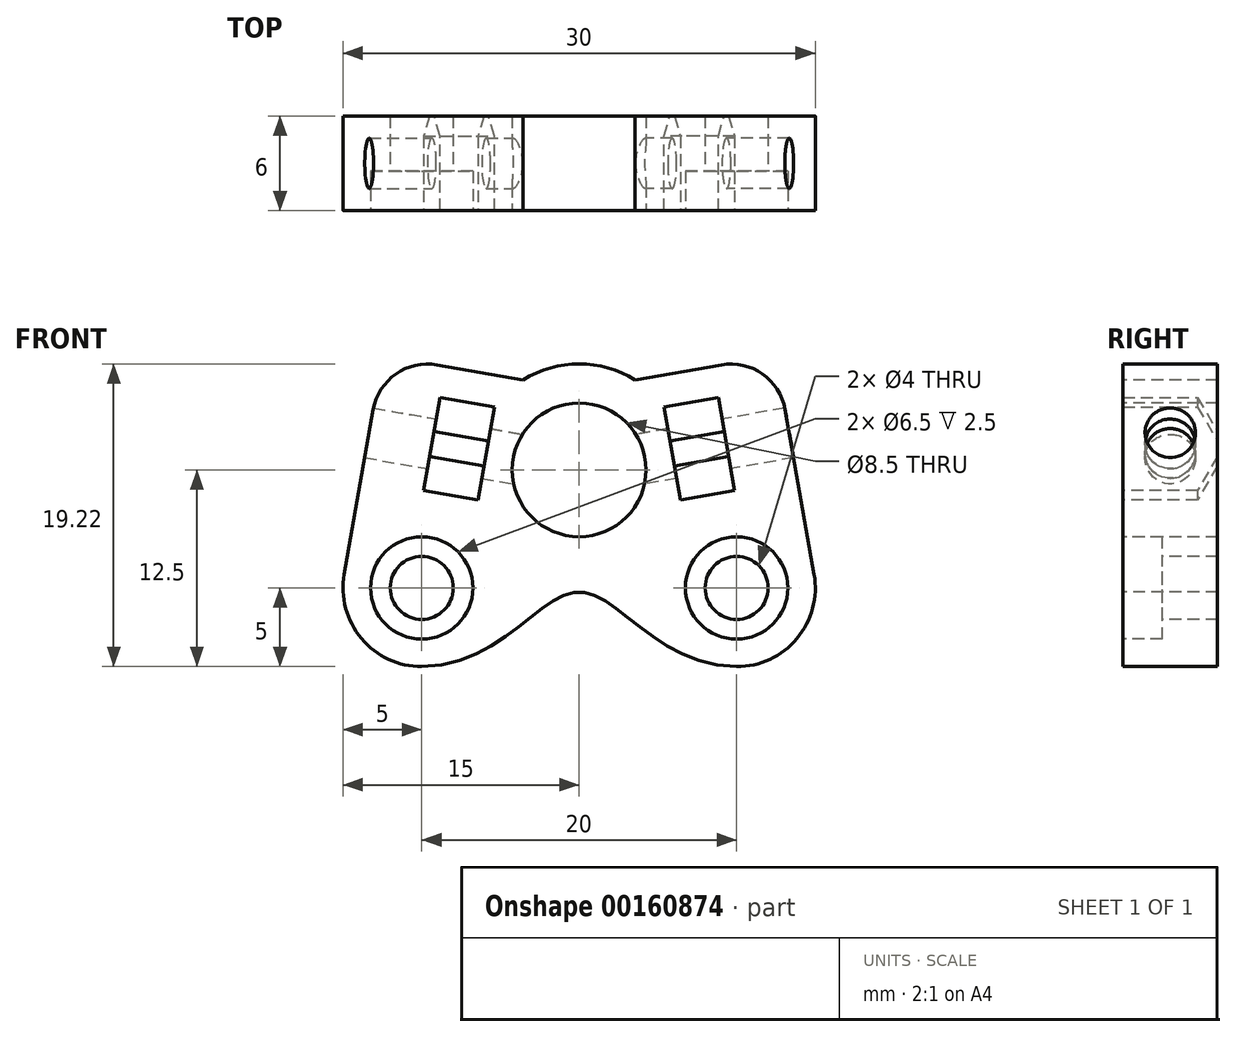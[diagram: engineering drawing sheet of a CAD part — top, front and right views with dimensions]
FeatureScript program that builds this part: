
annotation { "Feature Type Name" : "Feature", "Feature Type Description" : "" }
export const myFeature = defineFeature(function(context is Context, id is Id, definition is map)
    precondition{}
    {
        {
            var Q0;
            Q0=qCreatedBy(makeId("Front.planeOp"),FACE);
            var sketch = newSketch(context, id + "F0", { "sketchPlane" : qUnion([Q0])});
            skCircle(sketch, "E0", {"center": v(0, 0) * mm, "radius": 4.25 * mm});
            skCircle(sketch, "E1", {"center": v(-10, -7.5) * mm, "radius": 2 * mm});
            skCircle(sketch, "E2.MirrorC", {"center": v(10, -7.5) * mm, "radius": 2 * mm});
            skFitSpline(sketch, "E3", {"points": [v(10, -12.5) * mm, v(0, -7.75) * mm, v(-10, -12.5) * mm], "startDerivative": vector(-30, 0) * mm, "endDerivative": vector(-30, 0) * mm});
            skArc(sketch, "E4", {"start": v(10, -12.5) * mm, "mid": v(13.83, -10.71) * mm, "end": v(14.92, -6.63) * mm});
            skLineSegment(sketch, "E5", {"start": v(13.08, 3.83) * mm, "end": v(13.34, 2.35) * mm});
            skLineSegment(sketch, "E6", {"start": v(13.34, 2.35) * mm, "end": v(14.92, -6.63) * mm});
            skLineSegment(sketch, "E7", {"start": v(0, 0) * mm, "end": v(13.34, 2.35) * mm, "construction": true});
            skLineSegment(sketch, "E8.MirrorCS", {"start": v(-13.34, 2.35) * mm, "end": v(-14.92, -6.63) * mm});
            skLineSegment(sketch, "E9", {"start": v(9.02, 6.67) * mm, "end": v(3.56, 5.7) * mm});
            skArc(sketch, "E10", {"start": v(3.56, 5.7) * mm, "mid": v(1.85, 6.46) * mm, "end": v(0, 6.72) * mm});
            skArc(sketch, "E11.MirrorCS", {"start": v(-3.56, 5.7) * mm, "mid": v(-1.85, 6.46) * mm, "end": v(0, 6.72) * mm});
            skPoint(sketch, "E12.visualSharp", {"position": v(12.47, 7.28) * mm});
            skArc(sketch, "E12.filletArc", {"start": v(13.08, 3.83) * mm, "mid": v(11.64, 6.09) * mm, "end": v(9.02, 6.67) * mm});
            skArc(sketch, "E13.MirrorCS", {"start": v(-13.08, 3.83) * mm, "mid": v(-11.64, 6.09) * mm, "end": v(-9.02, 6.67) * mm});
            skLineSegment(sketch, "E14.MirrorCS", {"start": v(-9.02, 6.67) * mm, "end": v(-3.56, 5.7) * mm});
            skLineSegment(sketch, "E15.MirrorCS", {"start": v(-13.08, 3.83) * mm, "end": v(-13.34, 2.35) * mm});
            skLineSegment(sketch, "E16", {"start": v(10, -7.5) * mm, "end": v(14.92, -6.63) * mm, "construction": true});
            skArc(sketch, "E17.MirrorCS", {"start": v(-10, -12.5) * mm, "mid": v(-13.83, -10.71) * mm, "end": v(-14.92, -6.63) * mm});
            skLineSegment(sketch, "E18", {"start": v(0, 6.72) * mm, "end": v(13.48, 6.72) * mm, "construction": true});
            skSolve(sketch);
        }
        {
            var Q0;
            Q0 = qSketchRegion(id + "F0", true);
            extrude(context, id + "F1", {"entities" : qUnion([Q0]), "oppositeDirection" : true, "depth" : 6 * mm});
        }
        {
            var Q0;
            Q0=qCreatedBy(makeId("Right.planeOp"),FACE);
            var sketch = newSketch(context, id + "F2", { "sketchPlane" : qUnion([Q0])});
            skLineSegment(sketch, "E19", {"start": v(-49.69, 0) * mm, "end": v(53.27, 0) * mm, "construction": true});
            skSolve(sketch);
        }
        {
            var Q0;
            Q0=sQuery(id+"F2.wireOp",EDGE,"E19");
            cPlane(context, id + "F3", {"entities" : qUnion([Q0]), "cplaneType" : CPlaneType.LINE_ANGLE, "offset" : 25 * mm, "angle" : 80 * degree, "width" : 150 * mm, "height" : 150 * mm});
        }
        {
            var Q0;
            Q0=qCreatedBy(id+"F3.planeOp",FACE);
            var sketch = newSketch(context, id + "F4", { "sketchPlane" : qUnion([Q0])});
            skCircle(sketch, "E20", {"center": v(3, 0) * mm, "radius": 1.6 * mm});
            skLineSegment(sketch, "E21", {"start": v(0, 0) * mm, "end": v(6, 0) * mm, "construction": true});
            skSolve(sketch);
        }
        {
            var Q0;
            Q0 = qSketchRegion(id + "F4", true);
            extrude(context, id + "F5", {"entities" : qUnion([Q0]), "depth" : 15 * mm});
        }
        {
            var Q0;
            Q0=qCreatedBy(id+"F3.planeOp",FACE);
            cPlane(context, id + "F6", {"entities" : qUnion([Q0]), "cplaneType" : CPlaneType.OFFSET, "offset" : 6 * mm, "width" : 150 * mm, "height" : 150 * mm});
        }
        {
            var Q0;
            Q0=qCreatedBy(id+"F6.planeOp",FACE);
            var sketch = newSketch(context, id + "F7", { "sketchPlane" : qUnion([Q0])});
            skPoint(sketch, "E22", {"position": v(3, 0) * mm});
            skCircle(sketch, "E23.cCircle", {"center": v(3, 0) * mm, "radius": 3 * mm, "construction": true});
            skLineSegment(sketch, "E23.0", {"start": v(4.73, -3) * mm, "end": v(1.27, -3) * mm});
            skLineSegment(sketch, "E23.3", {"start": v(1.27, 3) * mm, "end": v(4.73, 3) * mm});
            skLineSegment(sketch, "E23.4", {"start": v(4.73, 3) * mm, "end": v(6.46, 0) * mm});
            skLineSegment(sketch, "E23.5", {"start": v(6.46, 0) * mm, "end": v(4.73, -3) * mm});
            skPoint(sketch, "E23.0.midPoint", {"position": v(3, -3) * mm});
            skLineSegment(sketch, "E24", {"start": v(1.27, -3) * mm, "end": v(-12.08, -3) * mm});
            skLineSegment(sketch, "E25", {"start": v(-12.08, -3) * mm, "end": v(-12.08, 3) * mm});
            skLineSegment(sketch, "E26", {"start": v(-12.08, 3) * mm, "end": v(1.27, 3) * mm});
            skLineSegment(sketch, "E27", {"start": v(0, 0) * mm, "end": v(6, 0) * mm, "construction": true});
            skSolve(sketch);
        }
        {
            var Q0;
            Q0 = qSketchRegion(id + "F7", true);
            extrude(context, id + "F8", {"entities" : qUnion([Q0]), "depth" : 3.5 * mm});
        }
        {
            var Q0;
            Q0=makeQuery(id+"F5.opExtrude","SWEPT_BODY",BODY,{"disambiguationData":[OSD([sQuery(id+"F4.wireOp",EDGE,"E20")])]});
            var Q1;
            Q1=makeQuery(id+"F8.opExtrude","SWEPT_BODY",BODY,{"disambiguationData":[OSD([sQuery(id+"F7.wireOp",EDGE,"E23.0"),sQuery(id+"F7.wireOp",EDGE,"E23.3"),sQuery(id+"F7.wireOp",EDGE,"E23.4"),sQuery(id+"F7.wireOp",EDGE,"E23.5"),sQuery(id+"F7.wireOp",EDGE,"E24"),sQuery(id+"F7.wireOp",EDGE,"E25"),sQuery(id+"F7.wireOp",EDGE,"E26")])]});
            var Q2;
            Q2=qCreatedBy(makeId("Right.planeOp"),FACE);
            mirror(context, id + "F9", {"entities" : qUnion([Q0, Q1]), "mirrorPlane" : qUnion([Q2])});
        }
        {
            var Q0;
            Q0=makeQuery(id+"F8.opExtrude","SWEPT_BODY",BODY,{"disambiguationData":[OSD([sQuery(id+"F7.wireOp",EDGE,"E23.0"),sQuery(id+"F7.wireOp",EDGE,"E23.3"),sQuery(id+"F7.wireOp",EDGE,"E23.4"),sQuery(id+"F7.wireOp",EDGE,"E23.5"),sQuery(id+"F7.wireOp",EDGE,"E24"),sQuery(id+"F7.wireOp",EDGE,"E25"),sQuery(id+"F7.wireOp",EDGE,"E26")])]});
            var Q1;
            Q1=makeQuery(id+"F5.opExtrude","SWEPT_BODY",BODY,{"disambiguationData":[OSD([sQuery(id+"F4.wireOp",EDGE,"E20")])]});
            var Q2;
            Q2=makeQuery(id+"F9.opPattern","COPY",BODY,{"derivedFrom":makeQuery(id+"F5.opExtrude","SWEPT_BODY",BODY,{"disambiguationData":[OSD([sQuery(id+"F4.wireOp",EDGE,"E20")])]}),"instanceName":"1"});
            var Q3;
            Q3=makeQuery(id+"F9.opPattern","COPY",BODY,{"derivedFrom":makeQuery(id+"F8.opExtrude","SWEPT_BODY",BODY,{"disambiguationData":[OSD([sQuery(id+"F7.wireOp",EDGE,"E23.0"),sQuery(id+"F7.wireOp",EDGE,"E23.3"),sQuery(id+"F7.wireOp",EDGE,"E23.4"),sQuery(id+"F7.wireOp",EDGE,"E23.5"),sQuery(id+"F7.wireOp",EDGE,"E24"),sQuery(id+"F7.wireOp",EDGE,"E25"),sQuery(id+"F7.wireOp",EDGE,"E26")])]}),"instanceName":"1"});
            var Q4;
            Q4=makeQuery(id+"F1.opExtrude","SWEPT_BODY",BODY,{"disambiguationData":[OSD([sQuery(id+"F0.wireOp",EDGE,"E0"),sQuery(id+"F0.wireOp",EDGE,"E1"),sQuery(id+"F0.wireOp",EDGE,"E2.MirrorC"),sQuery(id+"F0.wireOp",EDGE,"E3"),sQuery(id+"F0.wireOp",EDGE,"E4"),sQuery(id+"F0.wireOp",EDGE,"E5"),sQuery(id+"F0.wireOp",EDGE,"E6"),sQuery(id+"F0.wireOp",EDGE,"128eeccf-823f-4dfa-9151-fa9b1aa3d3a30.MirrorCS"),sQuery(id+"F0.wireOp",EDGE,"E8.MirrorCS"),sQuery(id+"F0.wireOp",EDGE,"f4974d7c-0403-4914-b49d-29ec39c3c0f60.MirrorCS"),sQuery(id+"F0.wireOp",EDGE,"E9"),sQuery(id+"F0.wireOp",EDGE,"E10"),sQuery(id+"F0.wireOp",EDGE,"E11.MirrorCS"),sQuery(id+"F0.wireOp",EDGE,"56b4d959-372f-4972-9b38-cac70896ad9a0.MirrorCS")])]});
            booleanBodies(context, id + "F10", {"operationType" : BooleanOperationType.SUBTRACTION, "tools" : qUnion([Q0, Q1, Q2, Q3]), "targets" : qUnion([Q4])});
        }
        {
            var Q0;
            Q0=makeQuery(id+"F1.opExtrude","CAP_FACE",FACE,{"disambiguationData":[OSD([sQuery(id+"F0.wireOp",EDGE,"E0"),sQuery(id+"F0.wireOp",EDGE,"E1"),sQuery(id+"F0.wireOp",EDGE,"E2.MirrorC"),sQuery(id+"F0.wireOp",EDGE,"E3"),sQuery(id+"F0.wireOp",EDGE,"E4"),sQuery(id+"F0.wireOp",EDGE,"E5"),sQuery(id+"F0.wireOp",EDGE,"E6"),sQuery(id+"F0.wireOp",EDGE,"128eeccf-823f-4dfa-9151-fa9b1aa3d3a30.MirrorCS"),sQuery(id+"F0.wireOp",EDGE,"E8.MirrorCS"),sQuery(id+"F0.wireOp",EDGE,"f4974d7c-0403-4914-b49d-29ec39c3c0f60.MirrorCS"),sQuery(id+"F0.wireOp",EDGE,"E9"),sQuery(id+"F0.wireOp",EDGE,"E10"),sQuery(id+"F0.wireOp",EDGE,"E11.MirrorCS"),sQuery(id+"F0.wireOp",EDGE,"56b4d959-372f-4972-9b38-cac70896ad9a0.MirrorCS")])],"isStart":true});
            var sketch = newSketch(context, id + "F11", { "sketchPlane" : qUnion([Q0])});
            skCircle(sketch, "E28", {"center": v(-10, -7.5) * mm, "radius": 3.25 * mm});
            skCircle(sketch, "E29.MirrorC", {"center": v(10, -7.5) * mm, "radius": 3.25 * mm});
            skSolve(sketch);
        }
        {
            var Q0;
            Q0 = qSketchRegion(id + "F11", true);
            extrude(context, id + "F12", {"entities" : qUnion([Q0]), "operationType" : NewBodyOperationType.REMOVE, "oppositeDirection" : true, "depth" : 2.5 * mm});
        }
    });
